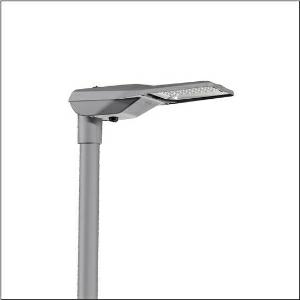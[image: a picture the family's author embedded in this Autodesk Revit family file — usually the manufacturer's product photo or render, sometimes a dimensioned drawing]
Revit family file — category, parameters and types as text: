
# Revit family: streetlight_sl_21_mini___pl52_5xe2h43t08gb_d0a8
name_source: partatom
category: Lighting Fixtures
units: mm (PartAtom-declared; Revit-internal decimal feet)

## family parameters
Cut with Voids When Loaded = No
Host = Face
Light Source = No
Part Type = Normal
Room Calculation Point = No
Round Connector Dimension = Use Diameter
Shared = No

## types (1)
- --- (1 x LED, 6080 lm, 40.4 W, 4000K)
    Apparent Load = 40 VA
    CIE Flux Codes = 27 59 98 100 100
    Color Rendering = 70
    Color Temperature = 4000K
    Default Elevation = 1800 mm
    Description = Streetlight SL 21 mini, mast luminaire, primary light control with lens, of PMMA, primary optical cover: cover, of toughened safety glass, transparent, light distribution: PL52, light emission: direct distribution, primary light characteristic: asymmetric, installation type: side-entry, post-top, LED, High Power LED, rated luminous flux: 6.080lm, luminous efficacy: 151lm/W, light colour: 740, colour temperature: 4000K, control gear: D4i, control: overheat protection, constant luminous flux control, time-dependent luminous flux control, flexible luminous flux parameterisation, pre-setting: logarithmic dimming characteristic, mains connection: 220..240V, AC, 50/60Hz, start of lifetime: 40W, end of service life: 41W, reduction: 19W, luminaire housing, of diecast aluminium, powder-coated, Siteco® metallic grey (DB 702S), corrosivity category C5 mid according to DIN EN ISO 12944, please order mast flange separately, inclination adjustable: 0°, 5°, 10°, 15°, sealing non-destructively replaceable, multi-level sealing system, length: 628mm, width: 235mm, height: 110mm, mast flange for spigot size: 42mm (side-entry): 5XC10008XM4, 60/48mm (side-entry/post-top): 5XC10108XM2, 76/60mm (side-entry/post-top): 5XC10108XM1, mounting height: 4..8m, Smart Interface below and above, protection rating (complete): IP66, insulation class (complete): insulation class II (safety insulation), certification: CE, ENEC, ENEC+, VDE, impact resistance: IK10, permissible operating ambient temperature for outdoor applications: -40..+50°C, standard-compliant lighting for roads and squares, packaging unit: 1 piece

Light Distribution: PL52
    Height = 110 mm
    Lamp = 1 x LED
    Lamp Light Flux = 6080 lm
    Lamp Power = 40.4 W
    Lamp count = 1
    Length = 625 mm
    Luminous efficacy = 151 lm/W
    Manufacturer = Siteco
    ModVariant = No
    Model = 5XE2H43T08GB
    Number of Poles = 1
    OnlyDefault = Yes
    Power Factor = 1
    Product Name = Streetlight SL 21 mini | PL52
    Product group = mast luminaire | pylon top
    ProductGroupID = 6100
    Protection Class = Protection class II
    Protection Degree = IP 66
    RLX_Detail_Level = 1
    RLX_Emergency_Light_Flux = 0 lm
    RLX_Emergency_Type = 0
    RLX_Emergency_Type_DB = No
    RlxData = <blob elided: 35945 chars, md5=20f13d1a>
    Socket = socket
    Standby Power = 0 W
    System Light Flux = 6080 lm
    System Power = 40 W
    Type Comments = factory setting: luminous flux: 100 % | dim-lin: 254 | 812 mA
    Type Image = l_1003514.jpg
    URL = http://relux.com
    VarID = @adj_190018
    Voltage = 0 V
    Weight = 0.00 kg
    Width = 234 mm

## geometry (parser evidence)
native form markers: Blend x4, Sweep x10
no freeform markers — native parametric forms only
